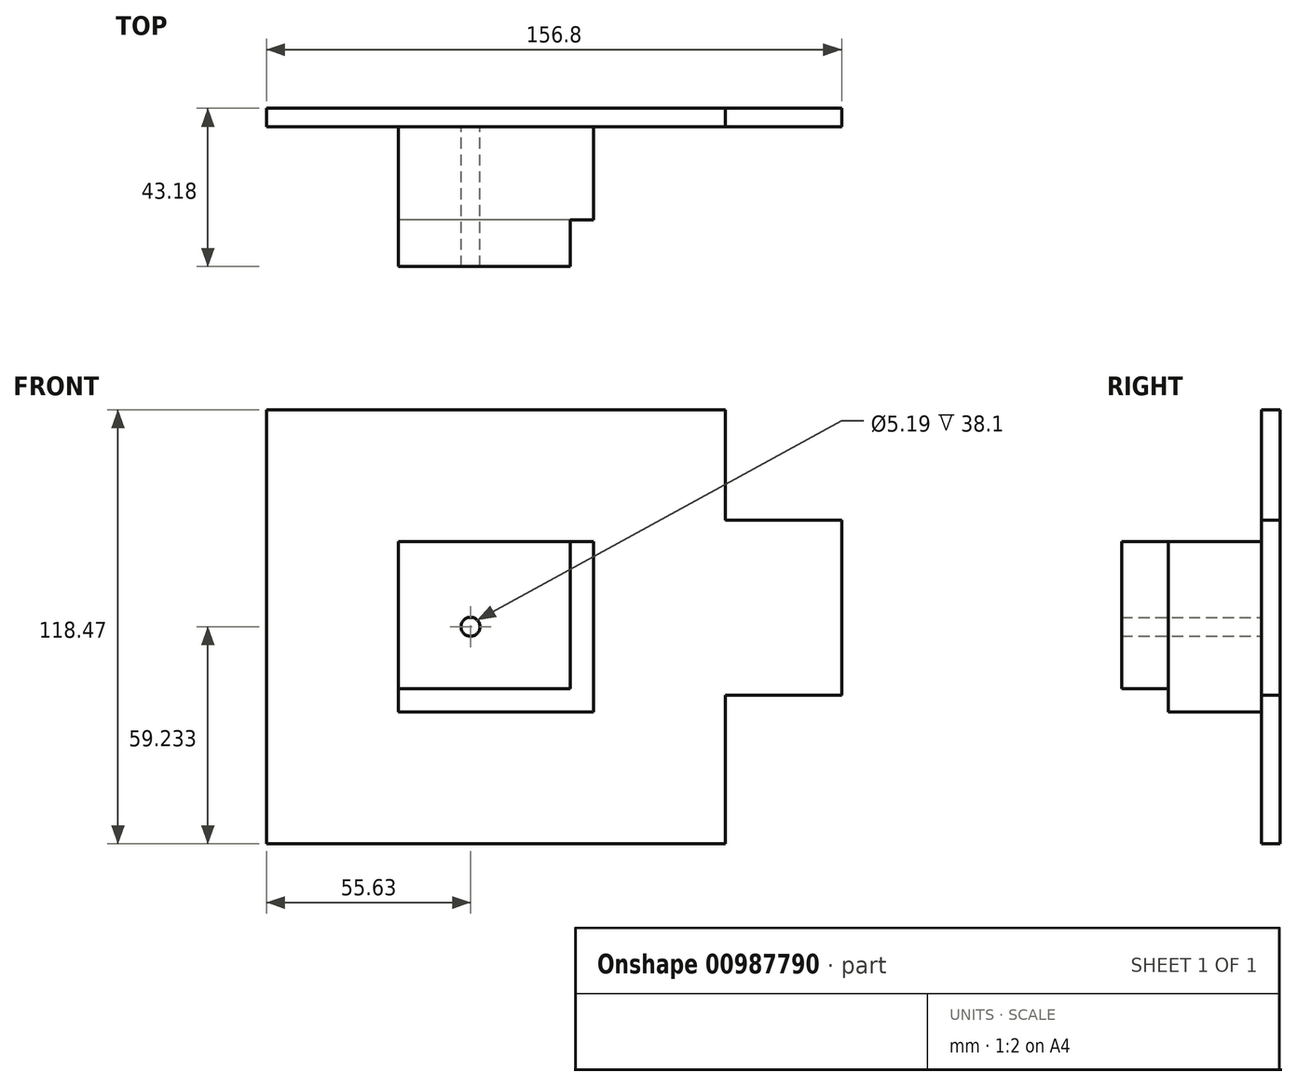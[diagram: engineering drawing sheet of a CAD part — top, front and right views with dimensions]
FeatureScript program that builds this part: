
annotation { "Feature Type Name" : "Feature", "Feature Type Description" : "" }
export const myFeature = defineFeature(function(context is Context, id is Id, definition is map)
    precondition{}
    {
        {
            var Q0;
            Q0=qCreatedBy(makeId("Front.planeOp"),FACE);
            var sketch = newSketch(context, id + "F0", { "sketchPlane" : qUnion([Q0])});
            skLineSegment(sketch, "E0.bottom", {"start": v(33.54, 37.47) * mm, "end": v(-19.64, 37.47) * mm});
            skLineSegment(sketch, "E0.top", {"start": v(33.54, -9.02) * mm, "end": v(-19.64, -9.02) * mm});
            skLineSegment(sketch, "E0.left", {"start": v(33.54, 37.47) * mm, "end": v(33.54, -9.02) * mm});
            skLineSegment(sketch, "E0.right", {"start": v(-19.64, 37.47) * mm, "end": v(-19.64, -9.02) * mm});
            skCircle(sketch, "E1", {"center": v(0, 14.22) * mm, "radius": 2.6 * mm});
            skPoint(sketch, "E1.centerSnap0", {"position": v(33.54, 14.22) * mm});
            skSolve(sketch);
        }
        {
            var Q0;
            Q0=makeQuery(id+"F0.imprint","IMPRINT",FACE,{"disambiguationData":[TD([[makeQuery(id+"F0.imprint","IMPRINT",EDGE,{"derivedFrom":sQuery(id+"F0.wireOp",EDGE,"E0.bottom")}),1.0]])]});
            extrude(context, id + "F1", {"entities" : qUnion([Q0]), "depth" : 25.4 * mm, "offsetDistance" : 25.4 * mm});
        }
        {
            var Q0;
            Q0=makeQuery(id+"F1.opExtrude","CAP_FACE",FACE,{"disambiguationData":[OSD([sQuery(id+"F0.wireOp",EDGE,"E0.bottom"),sQuery(id+"F0.wireOp",EDGE,"E0.top"),sQuery(id+"F0.wireOp",EDGE,"E0.left"),sQuery(id+"F0.wireOp",EDGE,"E0.right"),sQuery(id+"F0.wireOp",EDGE,"E1")])],"isStart":false});
            var sketch = newSketch(context, id + "F2", { "sketchPlane" : qUnion([Q0])});
            skPoint(sketch, "E2", {"position": v(14.36, 16.05) * mm});
            skLineSegment(sketch, "E3.0", {"start": v(27.19, -2.67) * mm, "end": v(-19.64, -2.67) * mm});
            skLineSegment(sketch, "E3.1", {"start": v(27.19, 37.47) * mm, "end": v(27.19, -2.67) * mm});
            skLineSegment(sketch, "E4.0", {"start": v(33.54, 43.82) * mm, "end": v(-19.64, 43.82) * mm});
            skSolve(sketch);
        }
        {
            var Q0;
            {var subQ4=sQuery(id+"F2.wireOp",EDGE,"E3.0");Q0=makeQuery(id+"F2.imprint","IMPRINT",FACE,{"disambiguationData":[TD([[makeQuery(id+"F2.imprint","IMPRINT",EDGE,{"derivedFrom":subQ4}),-1.0]])]});}
            extrude(context, id + "F3", {"entities" : qUnion([Q0]), "operationType" : NewBodyOperationType.ADD, "depth" : 12.7 * mm, "offsetDistance" : 25.4 * mm});
        }
        {
            var Q0;
            Q0=qCreatedBy(makeId("Front.planeOp"),FACE);
            var sketch = newSketch(context, id + "F4", { "sketchPlane" : qUnion([Q0])});
            skLineSegment(sketch, "E5.bottom", {"start": v(101.17, -4.47) * mm, "end": v(-26.62, -4.47) * mm});
            skLineSegment(sketch, "E5.top", {"start": v(101.17, 43.24) * mm, "end": v(-26.62, 43.24) * mm});
            skLineSegment(sketch, "E5.left", {"start": v(101.17, -4.47) * mm, "end": v(101.17, 43.24) * mm});
            skLineSegment(sketch, "E5.right", {"start": v(-26.62, -4.47) * mm, "end": v(-26.62, 43.24) * mm});
            skPoint(sketch, "E5.middle", {"position": v(37.27, 19.39) * mm});
            skLineSegment(sketch, "E6.bottom", {"start": v(115.74, -3.34) * mm, "end": v(107.9, -3.34) * mm});
            skLineSegment(sketch, "E6.top", {"start": v(115.74, 6.4) * mm, "end": v(107.9, 6.4) * mm});
            skLineSegment(sketch, "E6.left", {"start": v(115.74, -3.34) * mm, "end": v(115.74, 6.4) * mm});
            skLineSegment(sketch, "E6.right", {"start": v(107.9, -3.34) * mm, "end": v(107.9, 6.4) * mm});
            skPoint(sketch, "E6.middle", {"position": v(111.82, 1.53) * mm});
            skLineSegment(sketch, "E7.0", {"start": v(-55.63, 73.46) * mm, "end": v(-55.63, -45.01) * mm});
            skLineSegment(sketch, "E7.1", {"start": v(69.53, 73.46) * mm, "end": v(-55.63, 73.46) * mm});
            skLineSegment(sketch, "E7.2", {"start": v(69.53, 73.46) * mm, "end": v(69.53, -45.01) * mm});
            skLineSegment(sketch, "E7.3", {"start": v(69.53, -45.01) * mm, "end": v(-55.63, -45.01) * mm});
            skSolve(sketch);
        }
        {
            var Q0;
            Q0 = qSketchRegion(id + "F4", true);
            extrude(context, id + "F5", {"entities" : qUnion([Q0]), "operationType" : NewBodyOperationType.ADD, "oppositeDirection" : true, "depth" : 5.08 * mm, "offsetDistance" : 25.4 * mm});
        }
        {
            var Q0;
            Q0=makeQuery(id+"F5.opExtrude","SWEPT_BODY",BODY,{"disambiguationData":[OSD([sQuery(id+"F4.wireOp",EDGE,"E6.bottom"),sQuery(id+"F4.wireOp",EDGE,"E6.top"),sQuery(id+"F4.wireOp",EDGE,"E6.left"),sQuery(id+"F4.wireOp",EDGE,"E6.right")])]});
            deleteBodies(context, id + "F6", {"entities" : qUnion([Q0])});
        }
    });
